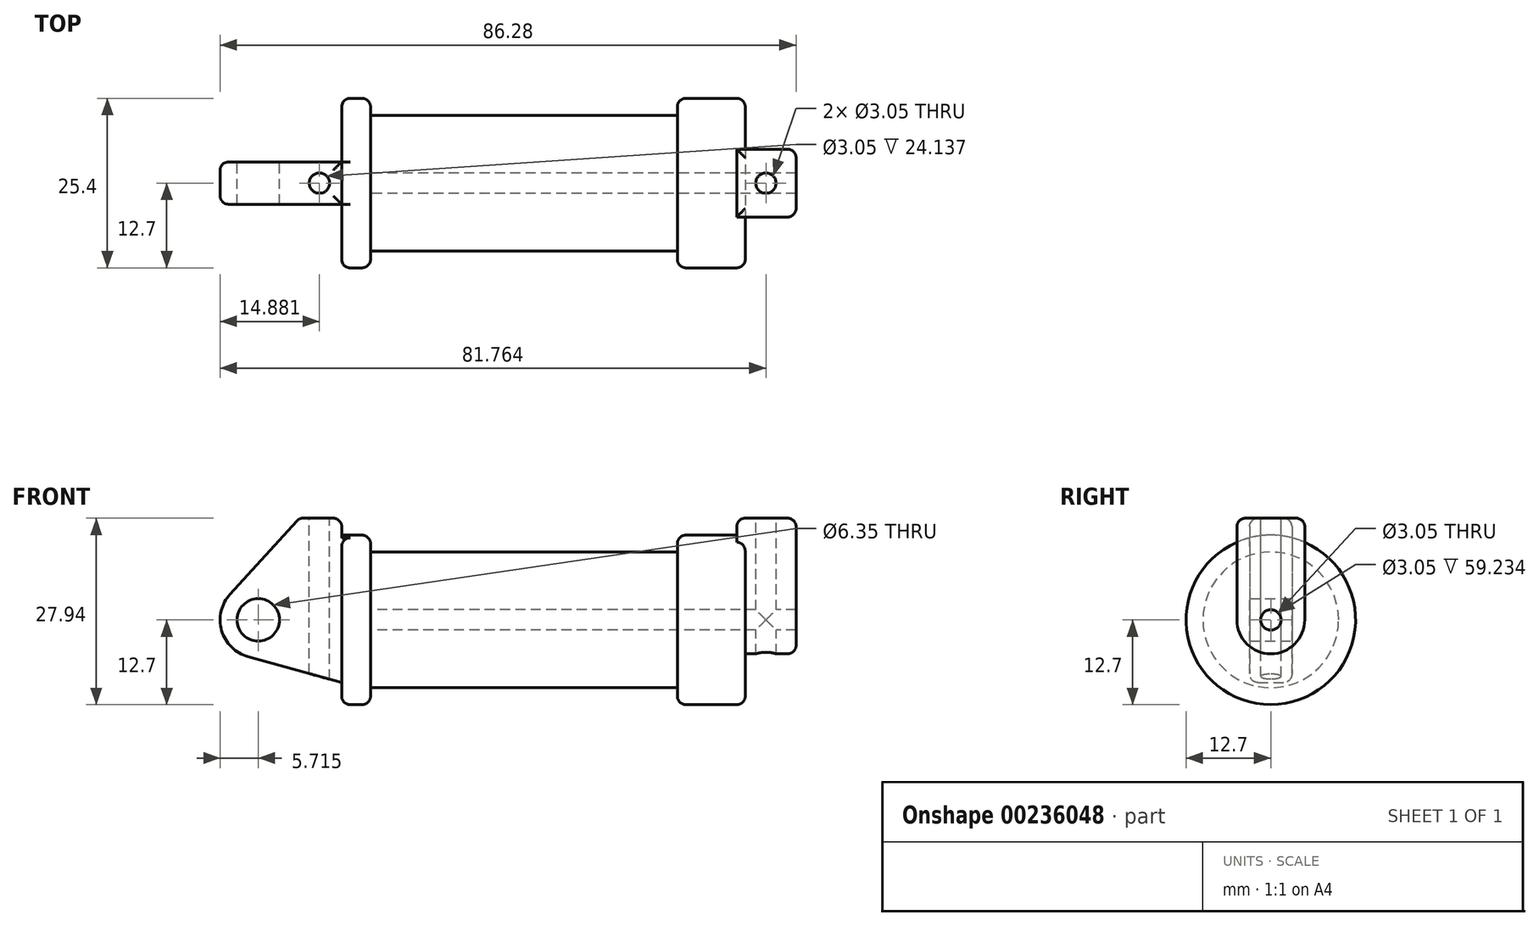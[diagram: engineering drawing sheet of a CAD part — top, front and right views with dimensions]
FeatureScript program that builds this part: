
annotation { "Feature Type Name" : "Feature", "Feature Type Description" : "" }
export const myFeature = defineFeature(function(context is Context, id is Id, definition is map)
    precondition{}
    {
        {
            var Q0;
            Q0=qCreatedBy(makeId("Front.planeOp"),FACE);
            var sketch = newSketch(context, id + "F0", { "sketchPlane" : qUnion([Q0])});
            skLineSegment(sketch, "E0", {"start": v(0, 0) * mm, "end": v(0, 12.7) * mm});
            skLineSegment(sketch, "E1", {"start": v(0, 12.7) * mm, "end": v(10.16, 12.7) * mm});
            skLineSegment(sketch, "E2", {"start": v(10.16, 12.7) * mm, "end": v(10.16, 10.16) * mm});
            skLineSegment(sketch, "E3", {"start": v(10.16, 10.16) * mm, "end": v(56.13, 10.16) * mm});
            skLineSegment(sketch, "E4", {"start": v(56.13, 10.16) * mm, "end": v(56.13, 12.7) * mm});
            skLineSegment(sketch, "E5", {"start": v(56.13, 12.7) * mm, "end": v(66.3, 12.7) * mm});
            skLineSegment(sketch, "E6", {"start": v(66.3, 12.7) * mm, "end": v(66.3, 0) * mm});
            skLineSegment(sketch, "E7", {"start": v(66.3, 0) * mm, "end": v(0, 0) * mm});
            skLineSegment(sketch, "E8", {"start": v(5.84, 15.24) * mm, "end": v(-0.5, 15.24) * mm});
            skLineSegment(sketch, "E9", {"start": v(-0.5, 15.24) * mm, "end": v(-10.88, 3.85) * mm});
            skLineSegment(sketch, "E10", {"start": v(0, 0) * mm, "end": v(-6.65, 0) * mm});
            skCircle(sketch, "E11", {"center": v(-6.65, 0) * mm, "radius": 5.72 * mm});
            skCircle(sketch, "E12", {"center": v(-6.65, 0) * mm, "radius": 3.18 * mm});
            skLineSegment(sketch, "E13", {"start": v(5.84, 15.24) * mm, "end": v(5.84, -9.4) * mm});
            skLineSegment(sketch, "E14", {"start": v(5.84, -9.4) * mm, "end": v(-8.18, -5.5) * mm});
            skSolve(sketch);
        }
        {
            var Q0;
            {var subQ0=sQuery(id+"F0.wireOp",EDGE,"E2");Q0=makeQuery(id+"F0.imprint","IMPRINT",FACE,{"disambiguationData":[TD([[makeQuery(id+"F0.imprint","IMPRINT",EDGE,{"derivedFrom":subQ0}),-1.0]])]});}
            var Q1;
            Q1=sQuery(id+"F0.wireOp",EDGE,"E7");
            revolve(context, id + "F1", {"entities" : qUnion([Q0]), "axis" : qUnion([Q1]), "revolveType" : RevolveType.FULL});
        }
        {
            var Q0;
            {var subQ0=sQuery(id+"F0.wireOp",EDGE,"E0");Q0=makeQuery(id+"F0.imprint","IMPRINT",FACE,{"disambiguationData":[TD([[makeQuery(id+"F0.imprint","IMPRINT",EDGE,{"derivedFrom":subQ0}),-1.0]])]});}
            var Q1;
            {var subQ0=sQuery(id+"F0.wireOp",EDGE,"E14");Q1=makeQuery(id+"F0.imprint","IMPRINT",FACE,{"disambiguationData":[TD([[makeQuery(id+"F0.imprint","IMPRINT",EDGE,{"derivedFrom":subQ0}),-1.0]])]});}
            var Q2;
            {var subQ4=sQuery(id+"F0.wireOp",EDGE,"E12");Q2=makeQuery(id+"F0.imprint","IMPRINT",FACE,{"disambiguationData":[TD([[makeQuery(id+"F0.imprint","IMPRINT",EDGE,{"derivedFrom":subQ4}),-1.0]])]});}
            var Q3;
            {var subQ3=sQuery(id+"F0.wireOp",EDGE,"E0");Q3=makeQuery(id+"F0.imprint","IMPRINT",FACE,{"disambiguationData":[TD([[makeQuery(id+"F0.imprint","IMPRINT",EDGE,{"derivedFrom":subQ3}),1.0]])]});}
            extrude(context, id + "F2", {"entities" : qUnion([Q0, Q1, Q2, Q3]), "operationType" : NewBodyOperationType.ADD, "endBound" : BoundingType.SYMMETRIC, "depth" : 6.35 * mm});
        }
        {
            var Q0;
            Q0=makeQuery(id+"F1.opRevolve","SWEPT_FACE",FACE,{"disambiguationData":[OSD([sQuery(id+"F0.wireOp",EDGE,"E6")])]});
            var sketch = newSketch(context, id + "F3", { "sketchPlane" : qUnion([Q0])});
            skCircle(sketch, "E15", {"center": v(0, 0) * mm, "radius": 1.52 * mm});
            skCircle(sketch, "E16", {"center": v(0, 0) * mm, "radius": 5.08 * mm});
            skLineSegment(sketch, "E17", {"start": v(-5.08, 0) * mm, "end": v(-5.08, 15.24) * mm});
            skLineSegment(sketch, "E18", {"start": v(5.08, 0) * mm, "end": v(5.08, 15.24) * mm});
            skLineSegment(sketch, "E19", {"start": v(-5.08, 15.24) * mm, "end": v(5.08, 15.24) * mm});
            skSolve(sketch);
        }
        {
            var Q0;
            {var subQ0=sQuery(id+"F3.wireOp",EDGE,"E19");Q0=makeQuery(id+"F3.imprint","IMPRINT",FACE,{"disambiguationData":[TD([[makeQuery(id+"F3.imprint","IMPRINT",EDGE,{"derivedFrom":subQ0}),-1.0]])]});}
            var Q1;
            {var subQ0=sQuery(id+"F3.wireOp",EDGE,"E17");var subQ1=sQuery(id+"F3.wireOp",EDGE,"E16");var subQ2=makeQuery(id+"F3.imprint","INTERSECT",VERTEX,{"derivedFrom":[subQ1,subQ0]});Q1=makeQuery(id+"F3.imprint","IMPRINT",FACE,{"disambiguationData":[TD([[makeQuery(id+"F3.imprint","IMPRINT",EDGE,{"disambiguationData":[TD([[subQ2,1.0]])],"derivedFrom":subQ1}),-1.0]])]});}
            var Q2;
            Q2=makeQuery(id+"F3.imprint","IMPRINT",FACE,{"disambiguationData":[TD([[makeQuery(id+"F3.imprint","IMPRINT",EDGE,{"derivedFrom":sQuery(id+"F3.wireOp",EDGE,"E15")}),-1.0]])]});
            extrude(context, id + "F4", {"entities" : qUnion([Q0, Q1, Q2]), "operationType" : NewBodyOperationType.ADD, "depth" : 7.62 * mm, "hasSecondDirection" : true, "secondDirectionOppositeDirection" : true, "secondDirectionDepth" : 1.27 * mm});
        }
        {
            var Q0;
            Q0=makeQuery(id+"F4.boolean.opBoolean","SPLIT",FACE,{"disambiguationData":[TD([makeQuery(id+"F4.opExtrude","SWEPT_FACE",FACE,{"disambiguationData":[OSD([sQuery(id+"F3.wireOp",EDGE,"E15")])]})])],"derivedFrom":makeQuery(id+"F1.opRevolve","SWEPT_FACE",FACE,{"disambiguationData":[OSD([sQuery(id+"F0.wireOp",EDGE,"E6")])]})});
            var Q1;
            Q1=makeQuery(id+"F1.opRevolve","SWEPT_FACE",FACE,{"disambiguationData":[OSD([sQuery(id+"F0.wireOp",EDGE,"E2")])]});
            extrude(context, id + "F5", {"entities" : qUnion([Q0]), "operationType" : NewBodyOperationType.REMOVE, "endBound" : BoundingType.UP_TO_SURFACE, "oppositeDirection" : true, "endBoundEntityFace" : qUnion([Q1]), "depth" : 25.4 * mm});
        }
        {
            var Q0;
            Q0=makeQuery(id+"F4.opExtrude","SWEPT_FACE",FACE,{"disambiguationData":[OSD([sQuery(id+"F3.wireOp",EDGE,"E19")])]});
            var sketch = newSketch(context, id + "F6", { "sketchPlane" : qUnion([Q0])});
            skCircle(sketch, "E20", {"center": v(69.4, 0) * mm, "radius": 1.52 * mm});
            skPoint(sketch, "E20.centerSnap0", {"position": v(65.02, 0) * mm});
            skCircle(sketch, "E21", {"center": v(2.51, 0) * mm, "radius": 1.52 * mm});
            skSolve(sketch);
        }
        {
            var Q0;
            Q0=makeQuery(id+"F6.imprint","IMPRINT",FACE,{"disambiguationData":[TD([[makeQuery(id+"F6.imprint","IMPRINT",EDGE,{"derivedFrom":sQuery(id+"F6.wireOp",EDGE,"E21")}),1.0]])]});
            extrude(context, id + "F7", {"entities" : qUnion([Q0]), "operationType" : NewBodyOperationType.REMOVE, "oppositeDirection" : true, "depth" : 17.78 * mm});
        }
        {
            var Q0;
            Q0 = qSketchRegion(id + "F6", true);
            extrude(context, id + "F8", {"entities" : qUnion([Q0]), "operationType" : NewBodyOperationType.REMOVE, "oppositeDirection" : true, "depth" : 1041.4 * mm});
        }
        {
            var Q0;
            Q0=makeQuery(id+"F1.opRevolve","SWEPT_EDGE",EDGE,{"disambiguationData":[OSD([sQuery(id+"F0.wireOp",EDGE,"E1"),sQuery(id+"F0.wireOp",EDGE,"E2")])]});
            var Q1;
            Q1=makeQuery(id+"F1.opRevolve","SWEPT_EDGE",EDGE,{"disambiguationData":[OSD([sQuery(id+"F0.wireOp",EDGE,"E4"),sQuery(id+"F0.wireOp",EDGE,"E5")])]});
            var Q2;
            Q2=makeQuery(id+"F2.opExtrude","SWEPT_EDGE",EDGE,{"disambiguationData":[OSD([sQuery(id+"F0.wireOp",EDGE,"E8"),sQuery(id+"F0.wireOp",EDGE,"E13")])]});
            var Q3;
            Q3=makeQuery(id+"F2.opExtrude","CAP_EDGE",EDGE,{"disambiguationData":[OSD([sQuery(id+"F0.wireOp",EDGE,"E8")])],"isStart":true});
            var Q4;
            Q4=makeQuery(id+"F2.opExtrude","SWEPT_EDGE",EDGE,{"disambiguationData":[OSD([sQuery(id+"F0.wireOp",EDGE,"E8"),sQuery(id+"F0.wireOp",EDGE,"E9")])]});
            var Q5;
            Q5=makeQuery(id+"F2.opExtrude","CAP_EDGE",EDGE,{"disambiguationData":[OSD([sQuery(id+"F0.wireOp",EDGE,"E8")])],"isStart":false});
            var Q6;
            {var subQ0=sQuery(id+"F0.wireOp",EDGE,"E1");var subQ1=sQuery(id+"F0.wireOp",EDGE,"E13");Q6=makeQuery(id+"F2.boolean.opBoolean","SPLIT",EDGE,{"disambiguationData":[topologyDisambiguationEdgeConnected([makeQuery(id+"F1.opRevolve","SWEPT_FACE",FACE,{"disambiguationData":[OSD([subQ1])]})])],"derivedFrom":makeQuery(id+"F1.opRevolve","SWEPT_EDGE",EDGE,{"disambiguationData":[OSD([subQ0,subQ1])]})});}
            var Q7;
            Q7=makeQuery(id+"F1.opRevolve","SWEPT_EDGE",EDGE,{"disambiguationData":[OSD([sQuery(id+"F0.wireOp",EDGE,"E5"),sQuery(id+"F0.wireOp",EDGE,"E6")])]});
            var Q8;
            Q8=makeQuery(id+"F2.opExtrude","CAP_EDGE",EDGE,{"disambiguationData":[OSD([sQuery(id+"F0.wireOp",EDGE,"E9")])],"isStart":false});
            var Q9;
            Q9=makeQuery(id+"F4.opExtrude","CAP_EDGE",EDGE,{"disambiguationData":[OSD([sQuery(id+"F3.wireOp",EDGE,"E17")])],"isStart":false});
            var Q10;
            Q10=makeQuery(id+"F4.opExtrude","CAP_EDGE",EDGE,{"disambiguationData":[OSD([sQuery(id+"F3.wireOp",EDGE,"E16")])],"isStart":false});
            var Q11;
            Q11=makeQuery(id+"F4.opExtrude","CAP_EDGE",EDGE,{"disambiguationData":[OSD([sQuery(id+"F3.wireOp",EDGE,"E18")])],"isStart":false});
            var Q12;
            Q12=makeQuery(id+"F4.opExtrude","CAP_EDGE",EDGE,{"disambiguationData":[OSD([sQuery(id+"F3.wireOp",EDGE,"E19")])],"isStart":false});
            var Q13;
            Q13=makeQuery(id+"F4.opExtrude","SWEPT_EDGE",EDGE,{"disambiguationData":[OSD([sQuery(id+"F3.wireOp",EDGE,"E17"),sQuery(id+"F3.wireOp",EDGE,"E19")])]});
            var Q14;
            Q14=makeQuery(id+"F4.opExtrude","SWEPT_EDGE",EDGE,{"disambiguationData":[OSD([sQuery(id+"F3.wireOp",EDGE,"E18"),sQuery(id+"F3.wireOp",EDGE,"E19")])]});
            var Q15;
            Q15=makeQuery(id+"F4.opExtrude","CAP_EDGE",EDGE,{"disambiguationData":[OSD([sQuery(id+"F3.wireOp",EDGE,"E19")])],"isStart":true});
            var Q16;
            Q16=makeQuery(id+"F2.opExtrude","CAP_EDGE",EDGE,{"disambiguationData":[OSD([sQuery(id+"F0.wireOp",EDGE,"E9")])],"isStart":true});
            var Q17;
            Q17=makeQuery(id+"F2.opExtrude","CAP_EDGE",EDGE,{"disambiguationData":[OSD([sQuery(id+"F0.wireOp",EDGE,"E11")])],"isStart":true});
            var Q18;
            Q18=makeQuery(id+"F2.opExtrude","CAP_EDGE",EDGE,{"disambiguationData":[OSD([sQuery(id+"F0.wireOp",EDGE,"E11")])],"isStart":false});
            fillet(context, id + "F9", {"entities" : qUnion([Q0, Q1, Q2, Q3, Q4, Q5, Q6, Q7, Q8, Q9, Q10, Q11, Q12, Q13, Q14, Q15, Q16, Q17, Q18]), "radius" : 1.27 * mm, "tangentPropagation" : true, "allowEdgeOverflow" : false});
        }
    });
